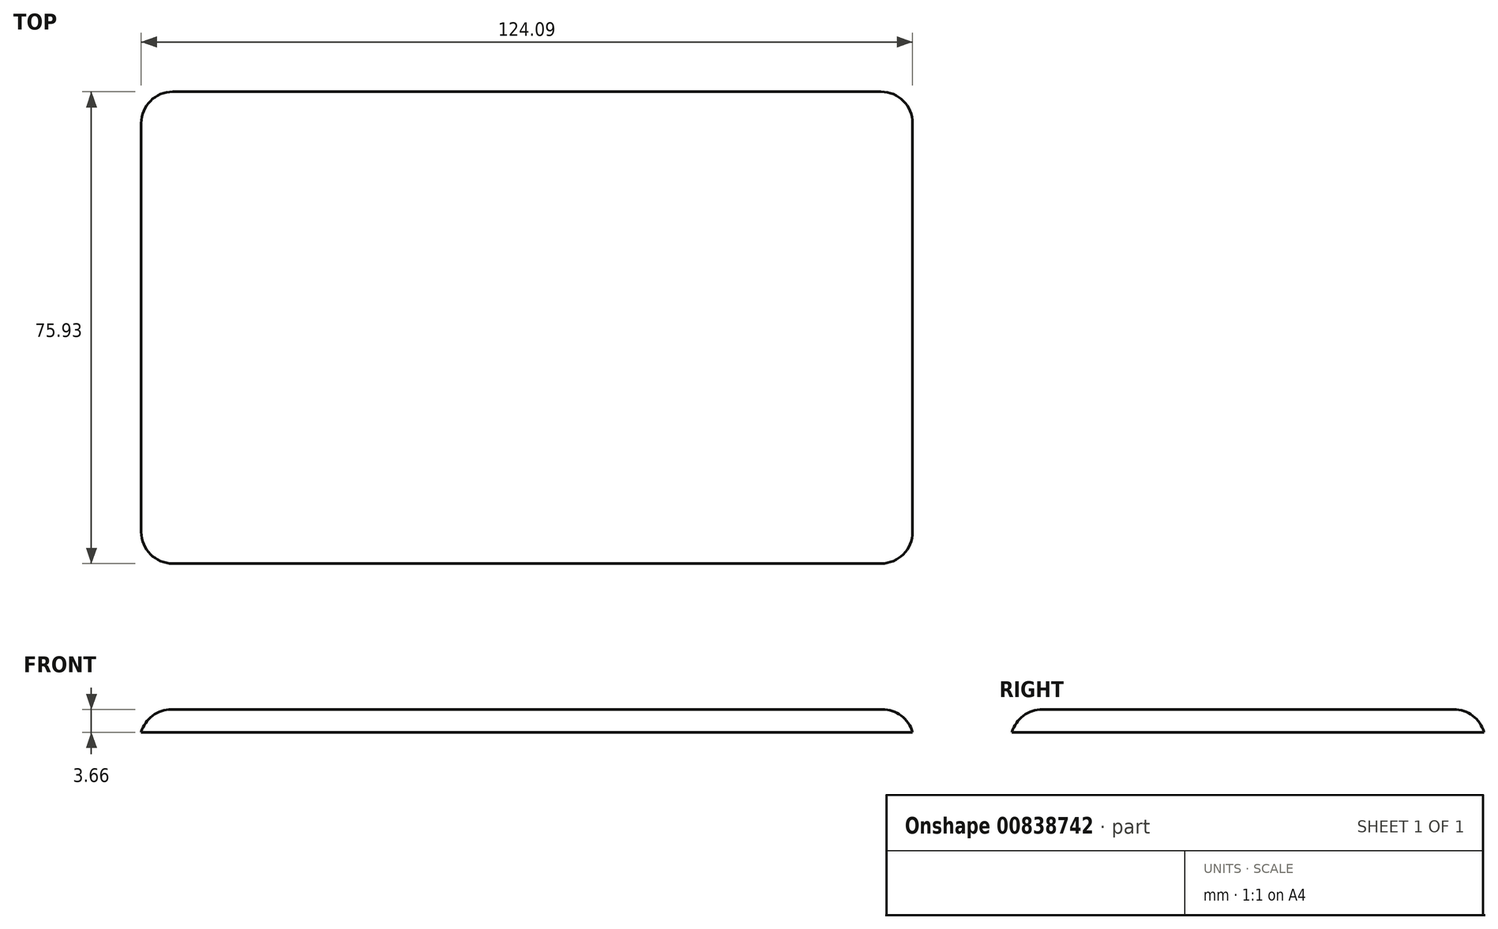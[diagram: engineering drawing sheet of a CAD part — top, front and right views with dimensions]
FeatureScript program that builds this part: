
annotation { "Feature Type Name" : "Feature", "Feature Type Description" : "" }
export const myFeature = defineFeature(function(context is Context, id is Id, definition is map)
    precondition{}
    {
        {
            var Q0;
            Q0=qCreatedBy(makeId("Top.planeOp"),FACE);
            var sketch = newSketch(context, id + "F0", { "sketchPlane" : qUnion([Q0])});
            skLineSegment(sketch, "E0.bottom", {"start": v(29.8, 46.94) * mm, "end": v(-94.29, 46.94) * mm});
            skLineSegment(sketch, "E0.top", {"start": v(29.8, -29) * mm, "end": v(-94.29, -29) * mm});
            skLineSegment(sketch, "E0.left", {"start": v(29.8, 46.94) * mm, "end": v(29.8, -29) * mm});
            skLineSegment(sketch, "E0.right", {"start": v(-94.29, 46.94) * mm, "end": v(-94.29, -29) * mm});
            skSolve(sketch);
        }
        {
            var Q0;
            Q0=makeQuery(id+"F0.imprint","IMPRINT",FACE,{"disambiguationData":[TD([[makeQuery(id+"F0.imprint","IMPRINT",EDGE,{"derivedFrom":sQuery(id+"F0.wireOp",EDGE,"E0.bottom")}),1.0]])]});
            extrude(context, id + "F1", {"entities" : qUnion([Q0]), "oppositeDirection" : true, "depth" : 3.66 * mm, "offsetDistance" : 25.4 * mm});
        }
        {
            var Q0;
            Q0=makeQuery(id+"F1.opExtrude","SWEPT_EDGE",EDGE,{"disambiguationData":[OSD([sQuery(id+"F0.wireOp",EDGE,"E0.bottom"),sQuery(id+"F0.wireOp",EDGE,"E0.left")])]});
            var Q1;
            Q1=makeQuery(id+"F1.opExtrude","SWEPT_EDGE",EDGE,{"disambiguationData":[OSD([sQuery(id+"F0.wireOp",EDGE,"E0.top"),sQuery(id+"F0.wireOp",EDGE,"E0.left")])]});
            var Q2;
            Q2=makeQuery(id+"F1.opExtrude","SWEPT_EDGE",EDGE,{"disambiguationData":[OSD([sQuery(id+"F0.wireOp",EDGE,"E0.bottom"),sQuery(id+"F0.wireOp",EDGE,"E0.right")])]});
            var Q3;
            Q3=makeQuery(id+"F1.opExtrude","SWEPT_EDGE",EDGE,{"disambiguationData":[OSD([sQuery(id+"F0.wireOp",EDGE,"E0.top"),sQuery(id+"F0.wireOp",EDGE,"E0.right")])]});
            fillet(context, id + "F2", {"entities" : qUnion([Q0, Q1, Q2, Q3]), "radius" : 5.08 * mm, "tangentPropagation" : true, "allowEdgeOverflow" : false});
        }
        {
            var Q0;
            {var subQ0=sQuery(id+"F0.wireOp",EDGE,"E0.right");var subQ1=sQuery(id+"F0.wireOp",EDGE,"E0.bottom");Q0=makeQuery(id+"F2.opFillet","BLEND_EDGE",EDGE,{"blendedFrom":[makeQuery(id+"F1.opExtrude","SWEPT_EDGE",EDGE,{"disambiguationData":[OSD([subQ1,subQ0])]}),makeQuery(id+"F1.opExtrude","CAP_FACE",FACE,{"disambiguationData":[OSD([subQ1,sQuery(id+"F0.wireOp",EDGE,"E0.top"),sQuery(id+"F0.wireOp",EDGE,"E0.left"),subQ0])],"isStart":true})],"blendedInto":[makeQuery(id+"F1.opExtrude","CAP_FACE",FACE,{"disambiguationData":[OSD([subQ1,sQuery(id+"F0.wireOp",EDGE,"E0.top"),sQuery(id+"F0.wireOp",EDGE,"E0.left"),subQ0])],"isStart":true})]});}
            fillet(context, id + "F3", {"entities" : qUnion([Q0]), "radius" : 5.08 * mm, "tangentPropagation" : true, "allowEdgeOverflow" : false});
        }
    });
